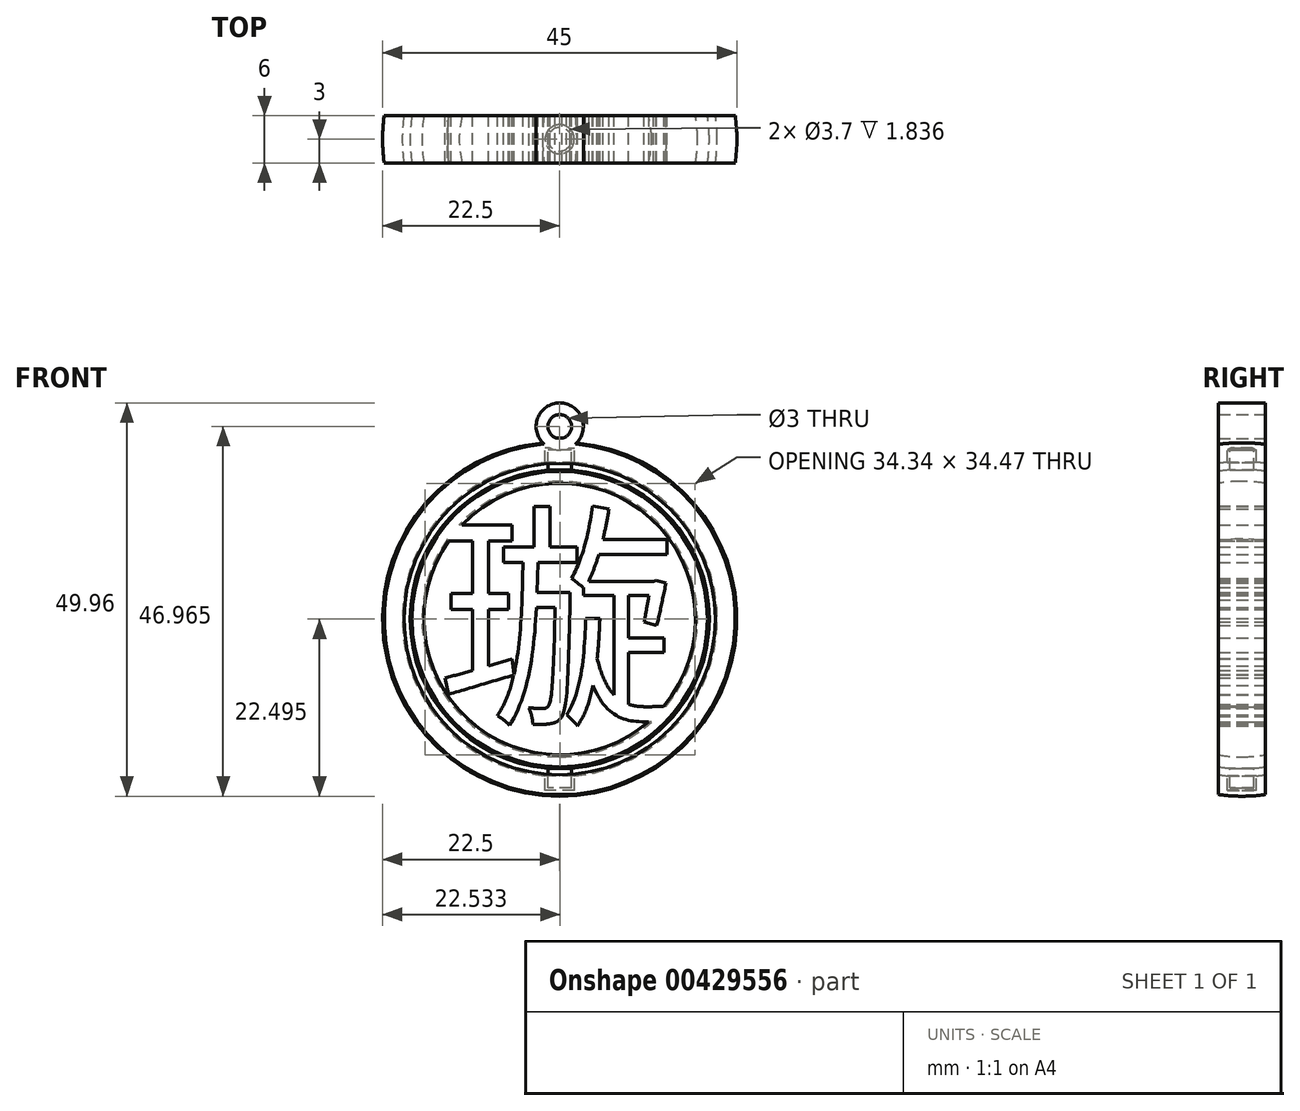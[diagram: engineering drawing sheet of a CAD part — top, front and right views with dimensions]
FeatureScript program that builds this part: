
annotation { "Feature Type Name" : "Feature", "Feature Type Description" : "" }
export const myFeature = defineFeature(function(context is Context, id is Id, definition is map)
    precondition{}
    {
        {
            var Q0;
            Q0=qCreatedBy(makeId("Front.planeOp"),FACE);
            var sketch = newSketch(context, id + "F0", { "sketchPlane" : qUnion([Q0])});
            skCircle(sketch, "E0", {"center": v(0, 0) * mm, "radius": 22.5 * mm});
            skCircle(sketch, "E1", {"center": v(0, 0) * mm, "radius": 20 * mm});
            skLineSegment(sketch, "E2.bottom", {"start": v(1.85, -21.75) * mm, "end": v(-1.85, -21.75) * mm});
            skLineSegment(sketch, "E2.top", {"start": v(1.85, 21.75) * mm, "end": v(-1.85, 21.75) * mm});
            skLineSegment(sketch, "E2.left", {"start": v(1.85, -21.75) * mm, "end": v(1.85, 21.75) * mm});
            skLineSegment(sketch, "E2.right", {"start": v(-1.85, -21.75) * mm, "end": v(-1.85, 21.75) * mm});
            skCircle(sketch, "E3", {"center": v(0, 0) * mm, "radius": 19 * mm});
            skCircle(sketch, "E4", {"center": v(0, 0) * mm, "radius": 17.5 * mm});
            skLineSegment(sketch, "E5.bottom", {"start": v(-1.5, -21.45) * mm, "end": v(1.5, -21.45) * mm});
            skLineSegment(sketch, "E5.top", {"start": v(-1.5, 21.45) * mm, "end": v(1.5, 21.45) * mm});
            skLineSegment(sketch, "E5.left", {"start": v(-1.5, -21.45) * mm, "end": v(-1.5, 21.45) * mm});
            skLineSegment(sketch, "E5.right", {"start": v(1.5, -21.45) * mm, "end": v(1.5, 21.45) * mm});
            skSolve(sketch);
        }
        {
            var Q0;
            Q0=qCreatedBy(makeId("Front.planeOp"),FACE);
            var sketch = newSketch(context, id + "F1", { "sketchPlane" : qUnion([Q0])});
            skCircle(sketch, "E6.0", {"center": v(0, 0) * mm, "radius": 22.5 * mm});
            skArc(sketch, "E6.1", {"start": v(-1.85, 19.91) * mm, "mid": v(-20, 0) * mm, "end": v(-1.85, -19.91) * mm});
            skLineSegment(sketch, "E6.2", {"start": v(1.85, -21.75) * mm, "end": v(-1.85, -21.75) * mm});
            skLineSegment(sketch, "E6.3", {"start": v(1.85, 21.75) * mm, "end": v(-1.85, 21.75) * mm});
            skLineSegment(sketch, "E6.4", {"start": v(1.85, -21.75) * mm, "end": v(1.85, -19.91) * mm});
            skLineSegment(sketch, "E6.5", {"start": v(-1.85, -21.75) * mm, "end": v(-1.85, -19.91) * mm});
            skPoint(sketch, "E6.6", {"position": v(0, 0) * mm});
            skArc(sketch, "E6.7", {"start": v(-1.5, 18.94) * mm, "mid": v(-19, 0) * mm, "end": v(-1.5, -18.94) * mm});
            skCircle(sketch, "E6.8", {"center": v(0, 0) * mm, "radius": 17.5 * mm});
            skLineSegment(sketch, "E6.9", {"start": v(-1.5, -21.45) * mm, "end": v(1.5, -21.45) * mm});
            skLineSegment(sketch, "E6.10", {"start": v(-1.5, 21.45) * mm, "end": v(1.5, 21.45) * mm});
            skLineSegment(sketch, "E6.11", {"start": v(-1.5, -21.45) * mm, "end": v(-1.5, -18.94) * mm});
            skLineSegment(sketch, "E6.12", {"start": v(1.5, -21.45) * mm, "end": v(1.5, -18.94) * mm});
            skPoint(sketch, "E6.13", {"position": v(0, 0) * mm});
            skLineSegment(sketch, "E7.trimOffspring", {"start": v(-1.85, 19.91) * mm, "end": v(-1.85, 21.75) * mm});
            skLineSegment(sketch, "E8.trimOffspring", {"start": v(1.85, 19.91) * mm, "end": v(1.85, 21.75) * mm});
            skLineSegment(sketch, "E9.trimOffspring", {"start": v(-1.5, 18.94) * mm, "end": v(-1.5, 21.45) * mm});
            skLineSegment(sketch, "E10.trimOffspring", {"start": v(1.5, 18.94) * mm, "end": v(1.5, 21.45) * mm});
            skArc(sketch, "E11.trimOffspring", {"start": v(1.85, -19.91) * mm, "mid": v(20, 0) * mm, "end": v(1.85, 19.91) * mm});
            skArc(sketch, "E12.trimOffspring", {"start": v(1.5, -18.94) * mm, "mid": v(19, 0) * mm, "end": v(1.5, 18.94) * mm});
            skSolve(sketch);
        }
        {
            var Q0;
            Q0=qCreatedBy(makeId("Front.planeOp"),FACE);
            var sketch = newSketch(context, id + "F2", { "sketchPlane" : qUnion([Q0])});
            skCircle(sketch, "E13.0", {"center": v(0, 0) * mm, "radius": 22.5 * mm});
            skArc(sketch, "E13.1", {"start": v(-1.85, 19.91) * mm, "mid": v(-20, 0) * mm, "end": v(-1.85, -19.91) * mm});
            skLineSegment(sketch, "E13.2", {"start": v(1.85, -21.75) * mm, "end": v(-1.85, -21.75) * mm});
            skLineSegment(sketch, "E13.3", {"start": v(1.85, 21.75) * mm, "end": v(-1.85, 21.75) * mm});
            skLineSegment(sketch, "E13.4", {"start": v(1.85, -21.75) * mm, "end": v(1.85, -19.91) * mm});
            skLineSegment(sketch, "E13.5", {"start": v(-1.85, -21.75) * mm, "end": v(-1.85, -19.91) * mm});
            skPoint(sketch, "E13.6", {"position": v(0, 0) * mm});
            skArc(sketch, "E13.7", {"start": v(-1.5, 18.94) * mm, "mid": v(-19, 0) * mm, "end": v(-1.5, -18.94) * mm});
            skCircle(sketch, "E13.8", {"center": v(0, 0) * mm, "radius": 17.5 * mm});
            skLineSegment(sketch, "E13.9", {"start": v(-1.5, -21.45) * mm, "end": v(1.5, -21.45) * mm});
            skLineSegment(sketch, "E13.10", {"start": v(-1.5, 21.45) * mm, "end": v(1.5, 21.45) * mm});
            skLineSegment(sketch, "E13.11", {"start": v(-1.5, -21.45) * mm, "end": v(-1.5, -18.94) * mm});
            skLineSegment(sketch, "E13.12", {"start": v(1.5, -21.45) * mm, "end": v(1.5, -18.94) * mm});
            skPoint(sketch, "E13.13", {"position": v(0, 0) * mm});
            skLineSegment(sketch, "E13.14", {"start": v(-1.85, 19.91) * mm, "end": v(-1.85, 21.75) * mm});
            skLineSegment(sketch, "E13.15", {"start": v(1.85, 19.91) * mm, "end": v(1.85, 21.75) * mm});
            skLineSegment(sketch, "E13.16", {"start": v(-1.5, 18.94) * mm, "end": v(-1.5, 21.45) * mm});
            skLineSegment(sketch, "E13.17", {"start": v(1.5, 18.94) * mm, "end": v(1.5, 21.45) * mm});
            skArc(sketch, "E13.18", {"start": v(1.85, -19.91) * mm, "mid": v(20, 0) * mm, "end": v(1.85, 19.91) * mm});
            skArc(sketch, "E13.19", {"start": v(1.5, -18.94) * mm, "mid": v(19, 0) * mm, "end": v(1.5, 18.94) * mm});
            skLineSegment(sketch, "E14", {"start": v(0, 22.5) * mm, "end": v(0, -22.5) * mm});
            skPoint(sketch, "E14.startSnap0", {"position": v(0, 21.75) * mm});
            skSolve(sketch);
        }
        {
            var Q0;
            Q0=qCreatedBy(makeId("Front.planeOp"),FACE);
            var sketch = newSketch(context, id + "F3", { "sketchPlane" : qUnion([Q0])});
            skArc(sketch, "E15.0", {"start": v(0, -22.5) * mm, "mid": v(22.5, 0) * mm, "end": v(0, 22.5) * mm});
            skLineSegment(sketch, "E15.2", {"start": v(1.85, -21.75) * mm, "end": v(0, -21.75) * mm});
            skLineSegment(sketch, "E15.3", {"start": v(1.85, 21.75) * mm, "end": v(0, 21.75) * mm});
            skLineSegment(sketch, "E15.4", {"start": v(1.85, -21.75) * mm, "end": v(1.85, -19.91) * mm});
            skPoint(sketch, "E15.6", {"position": v(0, 0) * mm});
            skArc(sketch, "E15.8", {"start": v(0, -17.5) * mm, "mid": v(17.5, 0) * mm, "end": v(0, 17.5) * mm});
            skLineSegment(sketch, "E15.9", {"start": v(0, -21.45) * mm, "end": v(1.5, -21.45) * mm});
            skLineSegment(sketch, "E15.10", {"start": v(0, 21.45) * mm, "end": v(1.5, 21.45) * mm});
            skLineSegment(sketch, "E15.12", {"start": v(1.5, -21.45) * mm, "end": v(1.5, -18.94) * mm});
            skPoint(sketch, "E15.13", {"position": v(0, 0) * mm});
            skLineSegment(sketch, "E15.15", {"start": v(1.85, 19.91) * mm, "end": v(1.85, 21.75) * mm});
            skLineSegment(sketch, "E15.17", {"start": v(1.5, 18.94) * mm, "end": v(1.5, 21.45) * mm});
            skArc(sketch, "E15.18", {"start": v(1.85, -19.91) * mm, "mid": v(20, 0) * mm, "end": v(1.85, 19.91) * mm});
            skArc(sketch, "E15.19", {"start": v(1.5, -18.94) * mm, "mid": v(19, 0) * mm, "end": v(1.5, 18.94) * mm});
            skLineSegment(sketch, "E15.20", {"start": v(0, 22.5) * mm, "end": v(0, 21.75) * mm});
            skPoint(sketch, "E15.21", {"position": v(0, 21.75) * mm});
            skPoint(sketch, "E15.11.end.orphan", {"position": v(-1.5, -18.94) * mm});
            skPoint(sketch, "E15.11.start.orphan", {"position": v(-1.5, -21.45) * mm});
            skPoint(sketch, "E15.5.end.orphan", {"position": v(-1.85, -19.91) * mm});
            skPoint(sketch, "E15.5.start.orphan", {"position": v(-1.85, -21.75) * mm});
            skPoint(sketch, "E15.1.end.orphan", {"position": v(-1.85, -19.91) * mm});
            skPoint(sketch, "E15.1.start.orphan", {"position": v(-1.85, 19.91) * mm});
            skPoint(sketch, "E15.7.end.orphan", {"position": v(-1.5, -18.94) * mm});
            skPoint(sketch, "E15.7.start.orphan", {"position": v(-1.5, 18.94) * mm});
            skLineSegment(sketch, "E16.trimOffspring", {"start": v(0, -21.75) * mm, "end": v(0, -22.5) * mm});
            skPoint(sketch, "E15.14.end.orphan", {"position": v(-1.85, 21.75) * mm});
            skPoint(sketch, "E15.14.start.orphan", {"position": v(-1.85, 19.91) * mm});
            skPoint(sketch, "E15.16.end.orphan", {"position": v(-1.5, 21.45) * mm});
            skPoint(sketch, "E15.16.start.orphan", {"position": v(-1.5, 18.94) * mm});
            skLineSegment(sketch, "E17.trimOffspring", {"start": v(0, 21.45) * mm, "end": v(0, 17.5) * mm});
            skLineSegment(sketch, "E18.trimOffspring", {"start": v(0, -17.5) * mm, "end": v(0, -21.45) * mm});
            skSolve(sketch);
        }
        {
            var Q0;
            Q0 = qSketchRegion(id + "F3", true);
            var Q1;
            Q1=sQuery(id+"F2.wireOp",EDGE,"E14");
            revolve(context, id + "F4", {"entities" : qUnion([Q0]), "axis" : qUnion([Q1]), "revolveType" : RevolveType.FULL});
        }
        {
            var Q0;
            Q0=qCreatedBy(makeId("Right.planeOp"),FACE);
            var sketch = newSketch(context, id + "F5", { "sketchPlane" : qUnion([Q0])});
            skLineSegment(sketch, "E19.bottom", {"start": v(3, 27.55) * mm, "end": v(36.37, 27.55) * mm});
            skLineSegment(sketch, "E19.top", {"start": v(3, -29.76) * mm, "end": v(36.37, -29.76) * mm});
            skLineSegment(sketch, "E19.left", {"start": v(3, 27.55) * mm, "end": v(3, -29.76) * mm});
            skLineSegment(sketch, "E19.right", {"start": v(36.37, 27.55) * mm, "end": v(36.37, -29.76) * mm});
            skLineSegment(sketch, "E20.MirrorCS", {"start": v(-3, 27.55) * mm, "end": v(-36.37, 27.55) * mm});
            skLineSegment(sketch, "E21.MirrorCS", {"start": v(-3, -29.76) * mm, "end": v(-36.37, -29.76) * mm});
            skLineSegment(sketch, "E22.MirrorCS", {"start": v(-3, 27.55) * mm, "end": v(-3, -29.76) * mm});
            skLineSegment(sketch, "E23.MirrorCS", {"start": v(-36.37, 27.55) * mm, "end": v(-36.37, -29.76) * mm});
            skSolve(sketch);
        }
        {
            var Q0;
            Q0 = qSketchRegion(id + "F5", true);
            extrude(context, id + "F6", {"entities" : qUnion([Q0]), "operationType" : NewBodyOperationType.REMOVE, "endBound" : BoundingType.SYMMETRIC, "oppositeDirection" : true, "depth" : 60 * mm});
        }
        {
            var Q0;
            Q0=qCreatedBy(makeId("Front.planeOp"),FACE);
            var sketch = newSketch(context, id + "F7", { "sketchPlane" : qUnion([Q0])});
            skCircle(sketch, "E24", {"center": v(0, 24.46) * mm, "radius": 3 * mm});
            skCircle(sketch, "E25", {"center": v(0, 24.46) * mm, "radius": 1.5 * mm});
            skSolve(sketch);
        }
        {
            var Q0;
            Q0 = qSketchRegion(id + "F7", true);
            extrude(context, id + "F8", {"entities" : qUnion([Q0]), "operationType" : NewBodyOperationType.ADD, "endBound" : BoundingType.SYMMETRIC, "depth" : 6 * mm});
        }
        {
            var Q0;
            Q0=qCreatedBy(makeId("Front.planeOp"),FACE);
            var sketch = newSketch(context, id + "F9", { "sketchPlane" : qUnion([Q0])});
            skText(sketch, "E26", { "text": "璇", "fontName": "NotoSansCJKjp-Regular.otf"});
            const initialGuessF9  = {"E26": [-0.01562, -0.01122, 1, 0, 0.022]};
            skSetInitialGuess(sketch, initialGuessF9);
            skSolve(sketch);
        }
        {
            var Q0;
            Q0 = qSketchRegion(id + "F9", true);
            extrude(context, id + "F10", {"entities" : qUnion([Q0]), "operationType" : NewBodyOperationType.ADD, "endBound" : BoundingType.SYMMETRIC, "depth" : 6 * mm});
        }
    });
